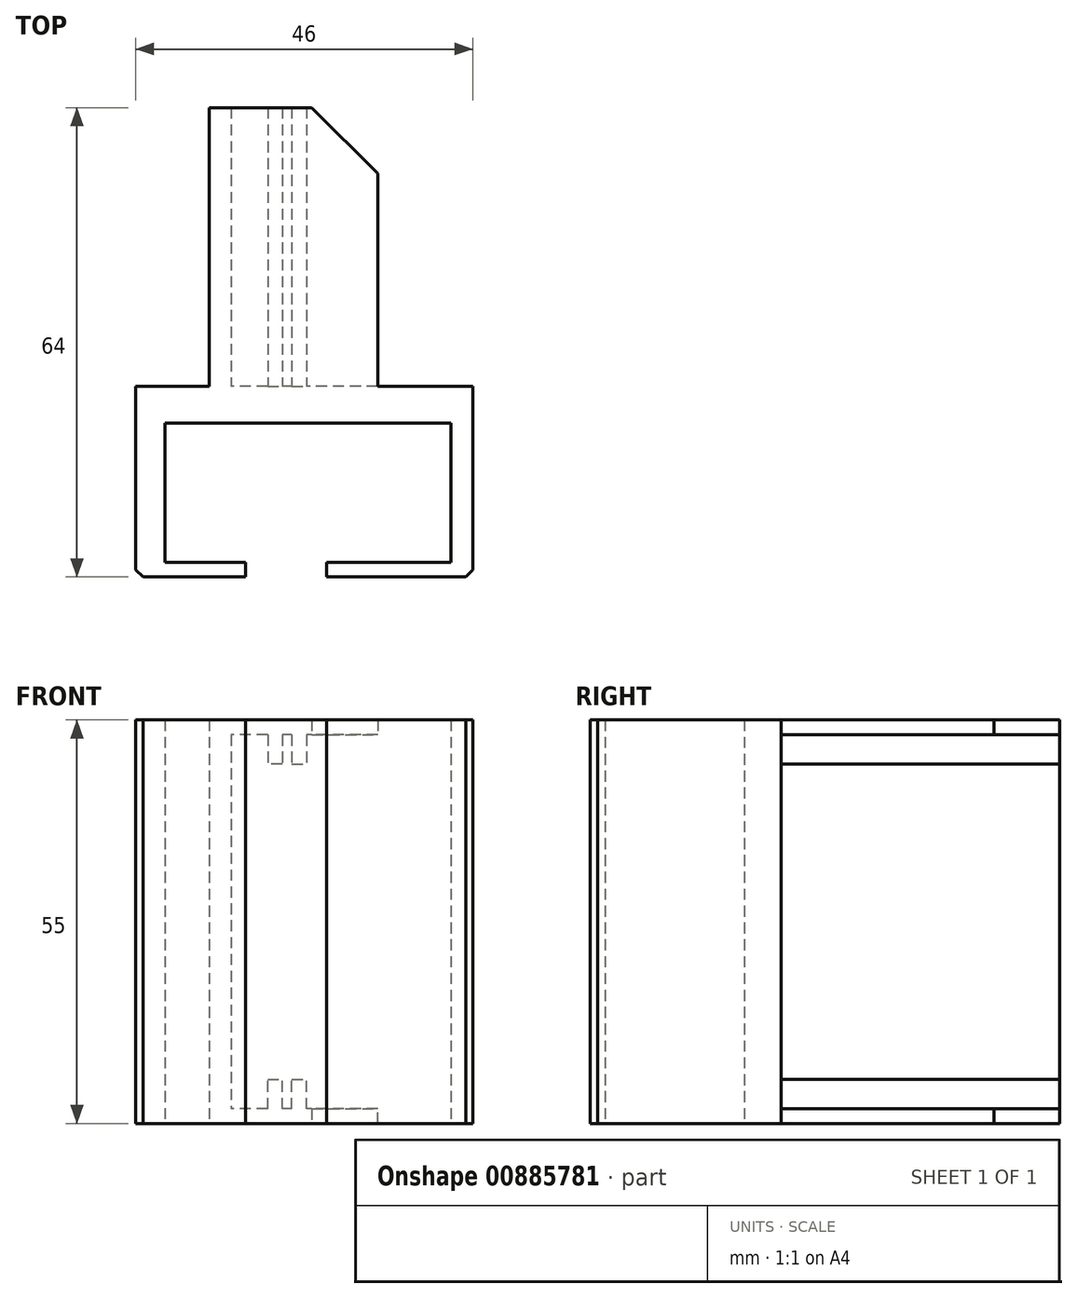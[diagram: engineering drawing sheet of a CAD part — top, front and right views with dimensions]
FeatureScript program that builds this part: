
annotation { "Feature Type Name" : "Feature", "Feature Type Description" : "" }
export const myFeature = defineFeature(function(context is Context, id is Id, definition is map)
    precondition{}
    {
        {
            var Q0;
            Q0=qCreatedBy(makeId("Top.planeOp"),FACE);
            var sketch = newSketch(context, id + "F0", { "sketchPlane" : qUnion([Q0])});
            skLineSegment(sketch, "E0.bottom", {"start": v(-46.84, 24) * mm, "end": v(-0.84, 24) * mm});
            skLineSegment(sketch, "E0.top", {"start": v(-46.84, 19) * mm, "end": v(-0.84, 19) * mm});
            skLineSegment(sketch, "E0.left", {"start": v(-46.84, 24) * mm, "end": v(-46.84, 19) * mm});
            skLineSegment(sketch, "E0.right", {"start": v(-0.84, 24) * mm, "end": v(-0.84, 19) * mm});
            skLineSegment(sketch, "E1.bottom", {"start": v(-46.84, 19) * mm, "end": v(-42.84, 19) * mm});
            skLineSegment(sketch, "E1.top", {"start": v(-46.84, 0) * mm, "end": v(-42.84, 0) * mm});
            skLineSegment(sketch, "E1.left", {"start": v(-46.84, 19) * mm, "end": v(-46.84, 0) * mm});
            skLineSegment(sketch, "E1.right", {"start": v(-42.84, 19) * mm, "end": v(-42.84, 0) * mm});
            skLineSegment(sketch, "E2.bottom", {"start": v(-46.84, 0) * mm, "end": v(-31.84, 0) * mm});
            skLineSegment(sketch, "E2.top", {"start": v(-46.84, -2) * mm, "end": v(-31.84, -2) * mm});
            skLineSegment(sketch, "E2.left", {"start": v(-46.84, 0) * mm, "end": v(-46.84, -2) * mm});
            skLineSegment(sketch, "E2.right", {"start": v(-31.84, 0) * mm, "end": v(-31.84, -2) * mm});
            skLineSegment(sketch, "E3.bottom", {"start": v(-0.84, 19) * mm, "end": v(-3.84, 19) * mm});
            skLineSegment(sketch, "E3.top", {"start": v(-0.84, 0) * mm, "end": v(-3.84, 0) * mm});
            skLineSegment(sketch, "E3.left", {"start": v(-0.84, 19) * mm, "end": v(-0.84, 0) * mm});
            skLineSegment(sketch, "E3.right", {"start": v(-3.84, 19) * mm, "end": v(-3.84, 0) * mm});
            skLineSegment(sketch, "E4.bottom", {"start": v(-0.84, 0) * mm, "end": v(-20.84, 0) * mm});
            skLineSegment(sketch, "E4.top", {"start": v(-0.84, -2) * mm, "end": v(-20.84, -2) * mm});
            skLineSegment(sketch, "E4.left", {"start": v(-0.84, 0) * mm, "end": v(-0.84, -2) * mm});
            skLineSegment(sketch, "E4.right", {"start": v(-20.84, 0) * mm, "end": v(-20.84, -2) * mm});
            skSolve(sketch);
        }
        {
            var Q0;
            Q0 = qSketchRegion(id + "F0", true);
            extrude(context, id + "F1", {"entities" : qUnion([Q0]), "depth" : 55 * mm, "offsetDistance" : 25 * mm});
        }
        {
            var Q0;
            Q0=makeQuery(id+"F1.opExtrude","SWEPT_FACE",FACE,{"disambiguationData":[OSD([sQuery(id+"F0.wireOp",EDGE,"E0.bottom")])]});
            var sketch = newSketch(context, id + "F2", { "sketchPlane" : qUnion([Q0])});
            skLineSegment(sketch, "E5.bottom", {"start": v(33.84, 55) * mm, "end": v(36.84, 55) * mm});
            skLineSegment(sketch, "E5.top", {"start": v(33.84, 0) * mm, "end": v(36.84, 0) * mm});
            skLineSegment(sketch, "E5.left", {"start": v(33.84, 55) * mm, "end": v(33.84, 0) * mm});
            skLineSegment(sketch, "E5.right", {"start": v(36.84, 55) * mm, "end": v(36.84, 0) * mm});
            skLineSegment(sketch, "E6.bottom", {"start": v(13.84, 55) * mm, "end": v(33.84, 55) * mm});
            skLineSegment(sketch, "E6.top", {"start": v(13.84, 53) * mm, "end": v(33.84, 53) * mm});
            skLineSegment(sketch, "E6.left", {"start": v(13.84, 55) * mm, "end": v(13.84, 53) * mm});
            skLineSegment(sketch, "E6.right", {"start": v(33.84, 55) * mm, "end": v(33.84, 53) * mm});
            skLineSegment(sketch, "E7.bottom", {"start": v(13.84, 0) * mm, "end": v(33.84, 0) * mm});
            skLineSegment(sketch, "E7.top", {"start": v(13.84, 2) * mm, "end": v(33.84, 2) * mm});
            skLineSegment(sketch, "E7.left", {"start": v(13.84, 0) * mm, "end": v(13.84, 2) * mm});
            skLineSegment(sketch, "E7.right", {"start": v(33.84, 0) * mm, "end": v(33.84, 2) * mm});
            skLineSegment(sketch, "E8.bottom", {"start": v(25.54, 53) * mm, "end": v(23.54, 53) * mm});
            skLineSegment(sketch, "E8.top", {"start": v(25.54, 49) * mm, "end": v(23.54, 49) * mm});
            skLineSegment(sketch, "E8.left", {"start": v(25.54, 53) * mm, "end": v(25.54, 49) * mm});
            skLineSegment(sketch, "E8.right", {"start": v(23.54, 53) * mm, "end": v(23.54, 49) * mm});
            skLineSegment(sketch, "E9.bottom", {"start": v(26.84, 53) * mm, "end": v(28.84, 53) * mm});
            skLineSegment(sketch, "E9.top", {"start": v(26.84, 49) * mm, "end": v(28.84, 49) * mm});
            skLineSegment(sketch, "E9.left", {"start": v(26.84, 53) * mm, "end": v(26.84, 49) * mm});
            skLineSegment(sketch, "E9.right", {"start": v(28.84, 53) * mm, "end": v(28.84, 49) * mm});
            skLineSegment(sketch, "E10.bottom", {"start": v(28.84, 2) * mm, "end": v(26.84, 2) * mm});
            skLineSegment(sketch, "E10.top", {"start": v(28.84, 6) * mm, "end": v(26.84, 6) * mm});
            skLineSegment(sketch, "E10.left", {"start": v(28.84, 2) * mm, "end": v(28.84, 6) * mm});
            skLineSegment(sketch, "E10.right", {"start": v(26.84, 2) * mm, "end": v(26.84, 6) * mm});
            skLineSegment(sketch, "E11.bottom", {"start": v(25.54, 2) * mm, "end": v(23.54, 2) * mm});
            skLineSegment(sketch, "E11.top", {"start": v(25.54, 6) * mm, "end": v(23.54, 6) * mm});
            skLineSegment(sketch, "E11.left", {"start": v(25.54, 2) * mm, "end": v(25.54, 6) * mm});
            skLineSegment(sketch, "E11.right", {"start": v(23.54, 2) * mm, "end": v(23.54, 6) * mm});
            skSolve(sketch);
        }
        {
            var Q0;
            Q0 = qSketchRegion(id + "F2", true);
            extrude(context, id + "F3", {"entities" : qUnion([Q0]), "operationType" : NewBodyOperationType.ADD, "depth" : 38 * mm, "offsetDistance" : 25 * mm});
        }
        {
            var Q0;
            Q0=makeQuery(id+"F3.opExtrude","CAP_EDGE",EDGE,{"disambiguationData":[OSD([sQuery(id+"F2.wireOp",EDGE,"E6.left")])],"isStart":false});
            var Q1;
            Q1=makeQuery(id+"F3.opExtrude","CAP_EDGE",EDGE,{"disambiguationData":[OSD([sQuery(id+"F2.wireOp",EDGE,"E7.left")])],"isStart":false});
            chamfer(context, id + "F4", {"entities" : qUnion([Q0, Q1]), "width" : 9 * mm, "tangentPropagation" : true});
        }
        {
            var Q0;
            Q0=makeQuery(id+"F1.opExtrude","SWEPT_EDGE",EDGE,{"disambiguationData":[OSD([sQuery(id+"F0.wireOp",EDGE,"E4.top"),sQuery(id+"F0.wireOp",EDGE,"E4.left")])]});
            var Q1;
            Q1=makeQuery(id+"F1.opExtrude","SWEPT_EDGE",EDGE,{"disambiguationData":[OSD([sQuery(id+"F0.wireOp",EDGE,"E2.top"),sQuery(id+"F0.wireOp",EDGE,"E2.left")])]});
            chamfer(context, id + "F5", {"entities" : qUnion([Q0, Q1]), "width" : 1 * mm, "tangentPropagation" : true});
        }
    });
